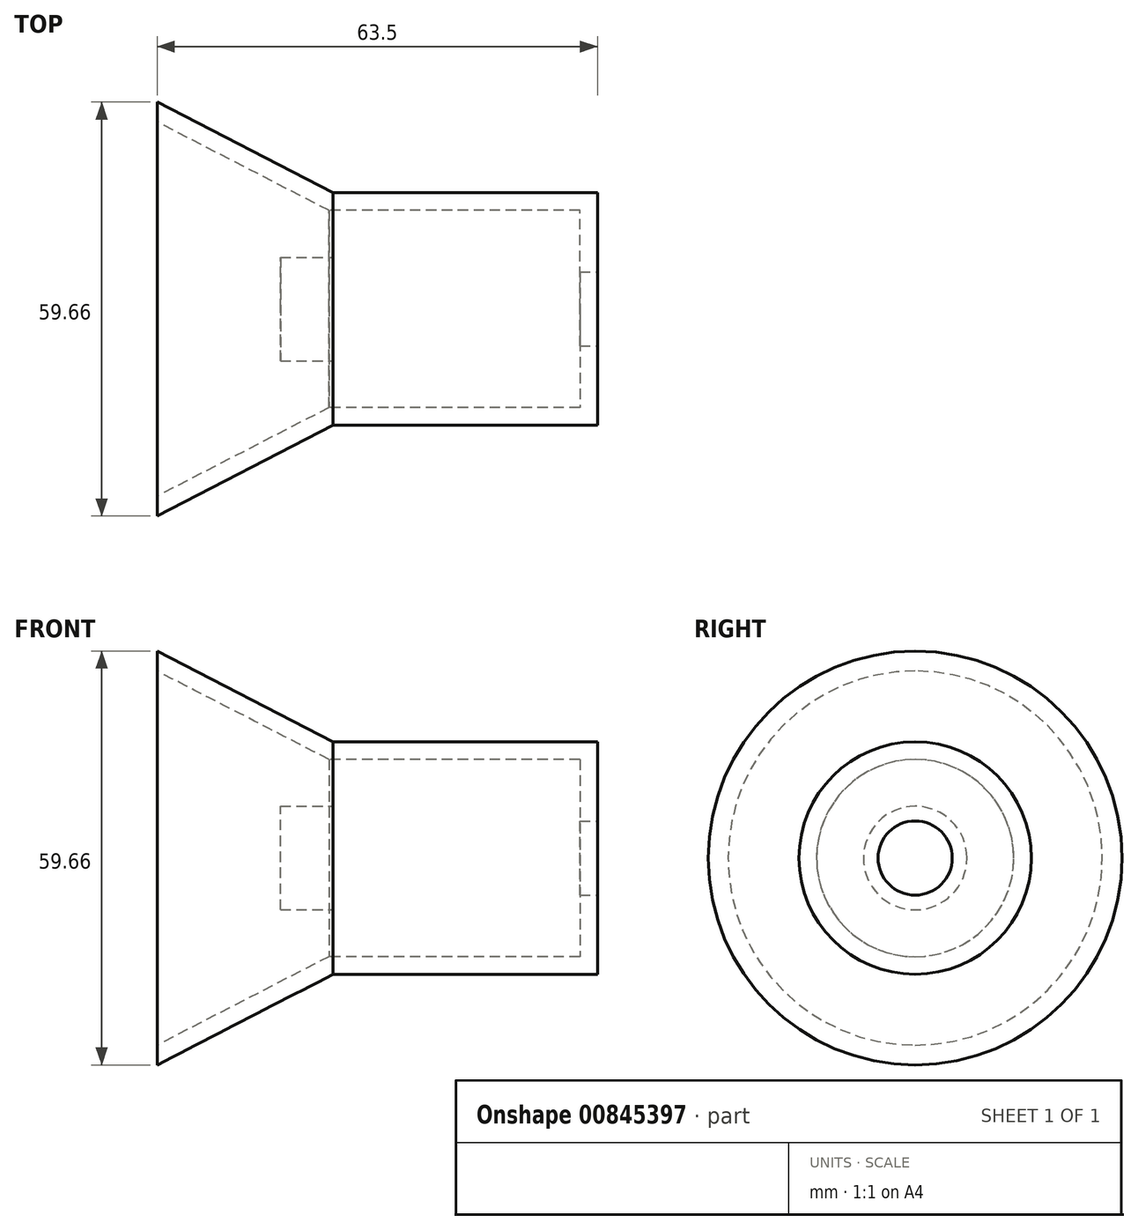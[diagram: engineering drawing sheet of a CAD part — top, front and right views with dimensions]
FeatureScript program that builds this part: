
annotation { "Feature Type Name" : "Feature", "Feature Type Description" : "" }
export const myFeature = defineFeature(function(context is Context, id is Id, definition is map)
    precondition{}
    {
        {
            var Q0;
            Q0=qCreatedBy(makeId("Right.planeOp"),FACE);
            var sketch = newSketch(context, id + "F0", { "sketchPlane" : qUnion([Q0])});
            skCircle(sketch, "E0", {"center": v(0, 0) * mm, "radius": 16.76 * mm});
            skSolve(sketch);
        }
        {
            var Q0;
            Q0=makeQuery(id+"F0.imprint","IMPRINT",FACE,{"disambiguationData":[TD([[makeQuery(id+"F0.imprint","IMPRINT",EDGE,{"derivedFrom":sQuery(id+"F0.wireOp",EDGE,"E0")}),1.0]])]});
            extrude(context, id + "F1", {"entities" : qUnion([Q0]), "depth" : 38.1 * mm, "offsetDistance" : 25.4 * mm});
        }
        {
            var Q0;
            Q0=qCreatedBy(makeId("Right.planeOp"),FACE);
            cPlane(context, id + "F2", {"entities" : qUnion([Q0]), "cplaneType" : CPlaneType.OFFSET, "offset" : 25.4 * mm, "oppositeDirection" : true, "width" : 152.4 * mm, "height" : 152.4 * mm});
        }
        {
            var Q0;
            Q0=qCreatedBy(id+"F2.planeOp",FACE);
            var sketch = newSketch(context, id + "F3", { "sketchPlane" : qUnion([Q0])});
            skCircle(sketch, "E1", {"center": v(0, 0) * mm, "radius": 29.83 * mm});
            skSolve(sketch);
        }
        {
            var Q1;
            Q1=makeQuery(id+"F1.opExtrude","CAP_FACE",FACE,{"disambiguationData":[OSD([sQuery(id+"F0.wireOp",EDGE,"E0")])],"isStart":true});
            var Q2;
            Q2=makeQuery(id+"F3.imprint","IMPRINT",FACE,{"disambiguationData":[TD([[makeQuery(id+"F3.imprint","IMPRINT",EDGE,{"derivedFrom":sQuery(id+"F3.wireOp",EDGE,"E1")}),1.0]])]});
            loft(context, id + "F4", {"operationType" : NewBodyOperationType.ADD, "sheetProfilesArray" : [{ "sheetProfileEntities" : qUnion([Q1]) }, { "sheetProfileEntities" : qUnion([Q2]) }]});
        }
        {
            var Q0;
            Q0=makeQuery(id+"F4.opLoft","CAP_FACE",FACE,{"disambiguationData":[OSD([makeQuery(id+"F3.imprint","IMPRINT",FACE,{"disambiguationData":[TD([[makeQuery(id+"F3.imprint","IMPRINT",EDGE,{"derivedFrom":sQuery(id+"F3.wireOp",EDGE,"E1")}),1.0]])]})])],"isStart":true});
            shell(context, id + "F5", {"entities" : qUnion([Q0]), "thickness" : 2.54 * mm});
        }
        {
            var Q0;
            Q0=makeQuery(id+"F1.opExtrude","CAP_FACE",FACE,{"disambiguationData":[OSD([sQuery(id+"F0.wireOp",EDGE,"E0")])],"isStart":false});
            var sketch = newSketch(context, id + "F6", { "sketchPlane" : qUnion([Q0])});
            skCircle(sketch, "E2", {"center": v(0, 0) * mm, "radius": 5.35 * mm});
            skSolve(sketch);
        }
        {
            var Q0;
            Q0=makeQuery(id+"F6.imprint","IMPRINT",FACE,{"disambiguationData":[TD([[makeQuery(id+"F6.imprint","IMPRINT",EDGE,{"derivedFrom":sQuery(id+"F6.wireOp",EDGE,"E2")}),1.0]])]});
            extrude(context, id + "F7", {"entities" : qUnion([Q0]), "operationType" : NewBodyOperationType.REMOVE, "oppositeDirection" : true, "depth" : 25.4 * mm, "offsetDistance" : 25.4 * mm});
        }
        {
            var Q0;
            Q0=qCreatedBy(makeId("Right.planeOp"),FACE);
            var sketch = newSketch(context, id + "F8", { "sketchPlane" : qUnion([Q0])});
            skCircle(sketch, "E3", {"center": v(0, 0) * mm, "radius": 7.46 * mm});
            skSolve(sketch);
        }
        {
            var Q0;
            Q0=makeQuery(id+"F8.imprint","IMPRINT",FACE,{"disambiguationData":[TD([[makeQuery(id+"F8.imprint","IMPRINT",EDGE,{"derivedFrom":sQuery(id+"F8.wireOp",EDGE,"E3")}),1.0]])]});
            extrude(context, id + "F9", {"entities" : qUnion([Q0]), "oppositeDirection" : true, "depth" : 7.62 * mm, "offsetDistance" : 25.4 * mm});
        }
    });
